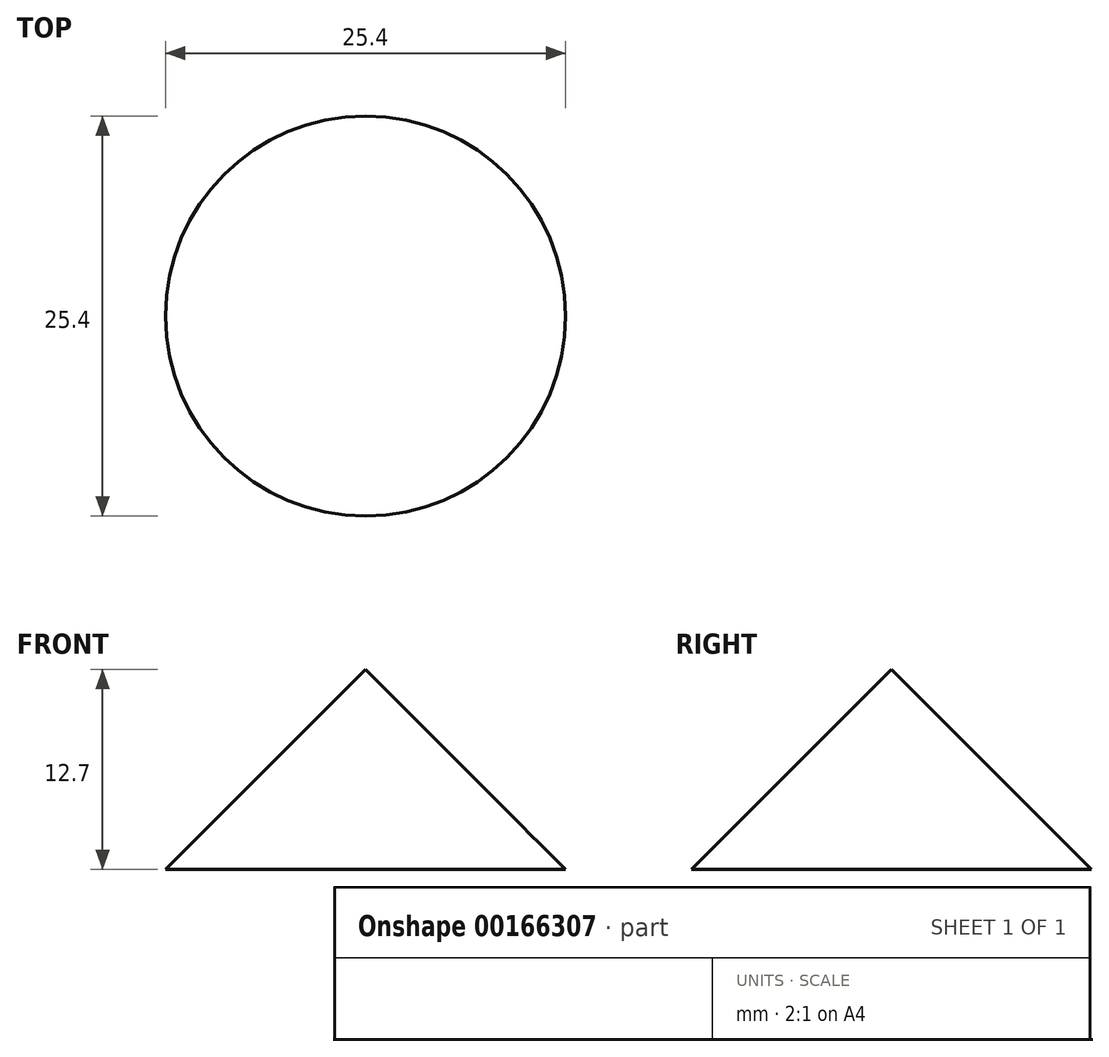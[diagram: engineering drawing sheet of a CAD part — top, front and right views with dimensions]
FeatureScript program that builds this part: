
annotation { "Feature Type Name" : "Feature", "Feature Type Description" : "" }
export const myFeature = defineFeature(function(context is Context, id is Id, definition is map)
    precondition{}
    {
        {
            var Q0;
            Q0=qCreatedBy(makeId("Top.planeOp"),FACE);
            var sketch = newSketch(context, id + "F0", { "sketchPlane" : qUnion([Q0])});
            skCircle(sketch, "E0", {"center": v(0, 0) * mm, "radius": 12.7 * mm});
            skSolve(sketch);
        }
        {
            var Q0;
            Q0=makeQuery(id+"F0.imprint","IMPRINT",FACE,{"disambiguationData":[TD([[makeQuery(id+"F0.imprint","IMPRINT",EDGE,{"derivedFrom":sQuery(id+"F0.wireOp",EDGE,"E0")}),1.0]])]});
            extrude(context, id + "F1", {"entities" : qUnion([Q0]), "depth" : 25.4 * mm, "hasDraft" : true, "draftAngle" : 45 * degree, "draftPullDirection" : true});
        }
    });
